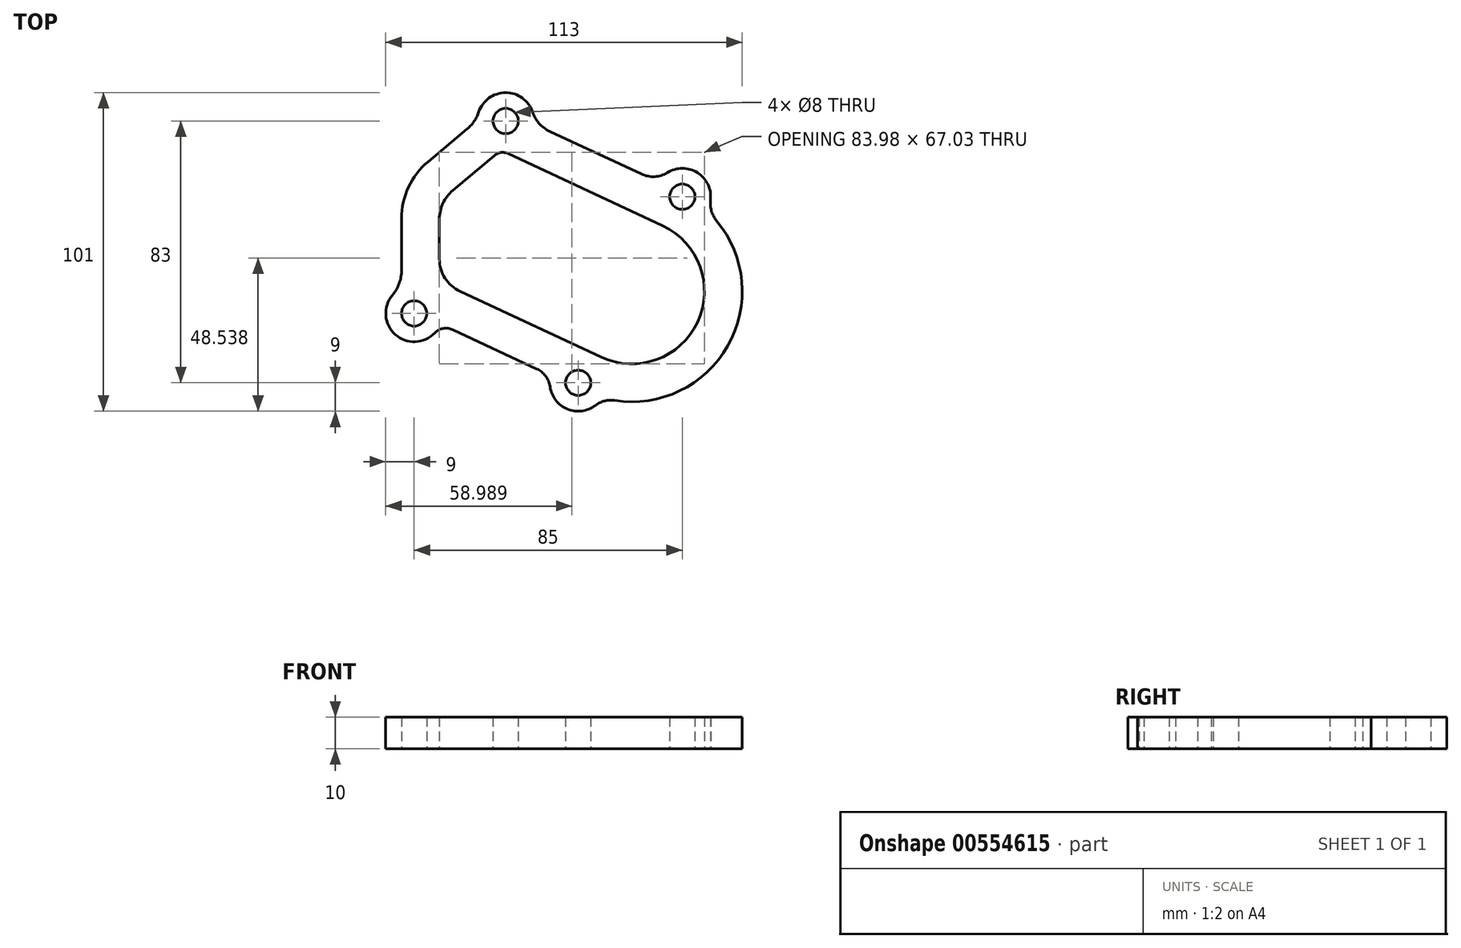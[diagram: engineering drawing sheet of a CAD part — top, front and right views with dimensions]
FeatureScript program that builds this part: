
annotation { "Feature Type Name" : "Feature", "Feature Type Description" : "" }
export const myFeature = defineFeature(function(context is Context, id is Id, definition is map)
    precondition{}
    {
        {
            var Q0;
            Q0=qCreatedBy(makeId("Top.planeOp"),FACE);
            var sketch = newSketch(context, id + "F0", { "sketchPlane" : qUnion([Q0])});
            skCircle(sketch, "E0", {"center": v(16, 30) * mm, "radius": 4 * mm});
            skCircle(sketch, "E1", {"center": v(-40, 54) * mm, "radius": 4 * mm});
            skLineSegment(sketch, "E2", {"start": v(-199.54, -60.76) * mm, "end": v(68.37, -60.76) * mm, "construction": true});
            skLineSegment(sketch, "E3", {"start": v(-129.38, -28.18) * mm, "end": v(-25.48, -76.62) * mm, "construction": true});
            skLineSegment(sketch, "E4", {"start": v(-199.68, -69.87) * mm, "end": v(-109.05, 6.17) * mm, "construction": true});
            skCircle(sketch, "E5", {"center": v(-17, -29) * mm, "radius": 4 * mm});
            skCircle(sketch, "E6", {"center": v(-69, -7) * mm, "radius": 4 * mm});
            skArc(sketch, "E7", {"start": v(-9.72, -20.85) * mm, "mid": v(20.85, -9.72) * mm, "end": v(9.72, 20.85) * mm});
            skLineSegment(sketch, "E8", {"start": v(-56.71, 32.04) * mm, "end": v(-43.51, 43.12) * mm});
            skLineSegment(sketch, "E9", {"start": v(9.72, 20.85) * mm, "end": v(-39.25, 43.68) * mm});
            skLineSegment(sketch, "E10", {"start": v(-9.72, -20.85) * mm, "end": v(-54.42, 0) * mm});
            skArc(sketch, "E11", {"start": v(-39.25, 43.68) * mm, "mid": v(-41.46, 44.02) * mm, "end": v(-43.51, 43.12) * mm});
            skLineSegment(sketch, "E12", {"start": v(-61, 22.85) * mm, "end": v(-61, 10.32) * mm});
            skArc(sketch, "E13", {"start": v(-56.71, 32.04) * mm, "mid": v(-59.88, 27.92) * mm, "end": v(-61, 22.85) * mm});
            skArc(sketch, "E14", {"start": v(-61, 10.32) * mm, "mid": v(-59.22, 4.2) * mm, "end": v(-54.42, 0) * mm});
            skArc(sketch, "E15", {"start": v(-31.47, 56.86) * mm, "mid": v(-40.02, 63) * mm, "end": v(-48.55, 56.82) * mm});
            skArc(sketch, "E16", {"start": v(-75.9, -1.23) * mm, "mid": v(-75, -13.7) * mm, "end": v(-62.5, -13.23) * mm});
            skArc(sketch, "E17", {"start": v(-25.91, -30.27) * mm, "mid": v(-20.4, -37.34) * mm, "end": v(-11.5, -36.13) * mm});
            skArc(sketch, "E18", {"start": v(11.27, 37.66) * mm, "mid": v(20.83, 37.6) * mm, "end": v(24.94, 28.96) * mm});
            skLineSegment(sketch, "E19", {"start": v(-26, 50.74) * mm, "end": v(3.08, 37.18) * mm});
            skLineSegment(sketch, "E20", {"start": v(-56.75, -12.16) * mm, "end": v(-30.14, -24.56) * mm});
            skLineSegment(sketch, "E21", {"start": v(-64.6, 41.1) * mm, "end": v(-52.1, 51.58) * mm});
            skLineSegment(sketch, "E22", {"start": v(-73, 23.07) * mm, "end": v(-73, 6.78) * mm});
            skArc(sketch, "E23", {"start": v(-64.6, 41.1) * mm, "mid": v(-70.8, 33.01) * mm, "end": v(-73, 23.07) * mm});
            skArc(sketch, "E24", {"start": v(-75.9, -1.23) * mm, "mid": v(-73.75, 2.52) * mm, "end": v(-73, 6.78) * mm});
            skArc(sketch, "E25", {"start": v(-56.75, -12.16) * mm, "mid": v(-59.8, -11.77) * mm, "end": v(-62.5, -13.23) * mm});
            skArc(sketch, "E26", {"start": v(-25.91, -30.27) * mm, "mid": v(-27.3, -26.88) * mm, "end": v(-30.14, -24.56) * mm});
            skArc(sketch, "E27", {"start": v(-52.1, 51.58) * mm, "mid": v(-49.96, 53.95) * mm, "end": v(-48.55, 56.82) * mm});
            skArc(sketch, "E28", {"start": v(-31.47, 56.86) * mm, "mid": v(-29.36, 53.24) * mm, "end": v(-26, 50.74) * mm});
            skArc(sketch, "E29", {"start": v(3.08, 37.18) * mm, "mid": v(7.24, 36.39) * mm, "end": v(11.27, 37.66) * mm});
            skArc(sketch, "E30", {"start": v(-5.43, -34.58) * mm, "mid": v(30.44, -17.27) * mm, "end": v(26.89, 22.4) * mm});
            skArc(sketch, "E31", {"start": v(24.94, 28.96) * mm, "mid": v(25.24, 25.48) * mm, "end": v(26.89, 22.4) * mm});
            skArc(sketch, "E32", {"start": v(-5.43, -34.58) * mm, "mid": v(-8.63, -34.73) * mm, "end": v(-11.5, -36.13) * mm});
            skSolve(sketch);
        }
        {
            var Q0;
            Q0=makeQuery(id+"F0.imprint","IMPRINT",FACE,{"disambiguationData":[TD([[makeQuery(id+"F0.imprint","IMPRINT",EDGE,{"derivedFrom":sQuery(id+"F0.wireOp",EDGE,"E0")}),-1.0]])]});
            extrude(context, id + "F1", {"entities" : qUnion([Q0]), "depth" : 10 * mm, "offsetDistance" : 25 * mm});
        }
    });
